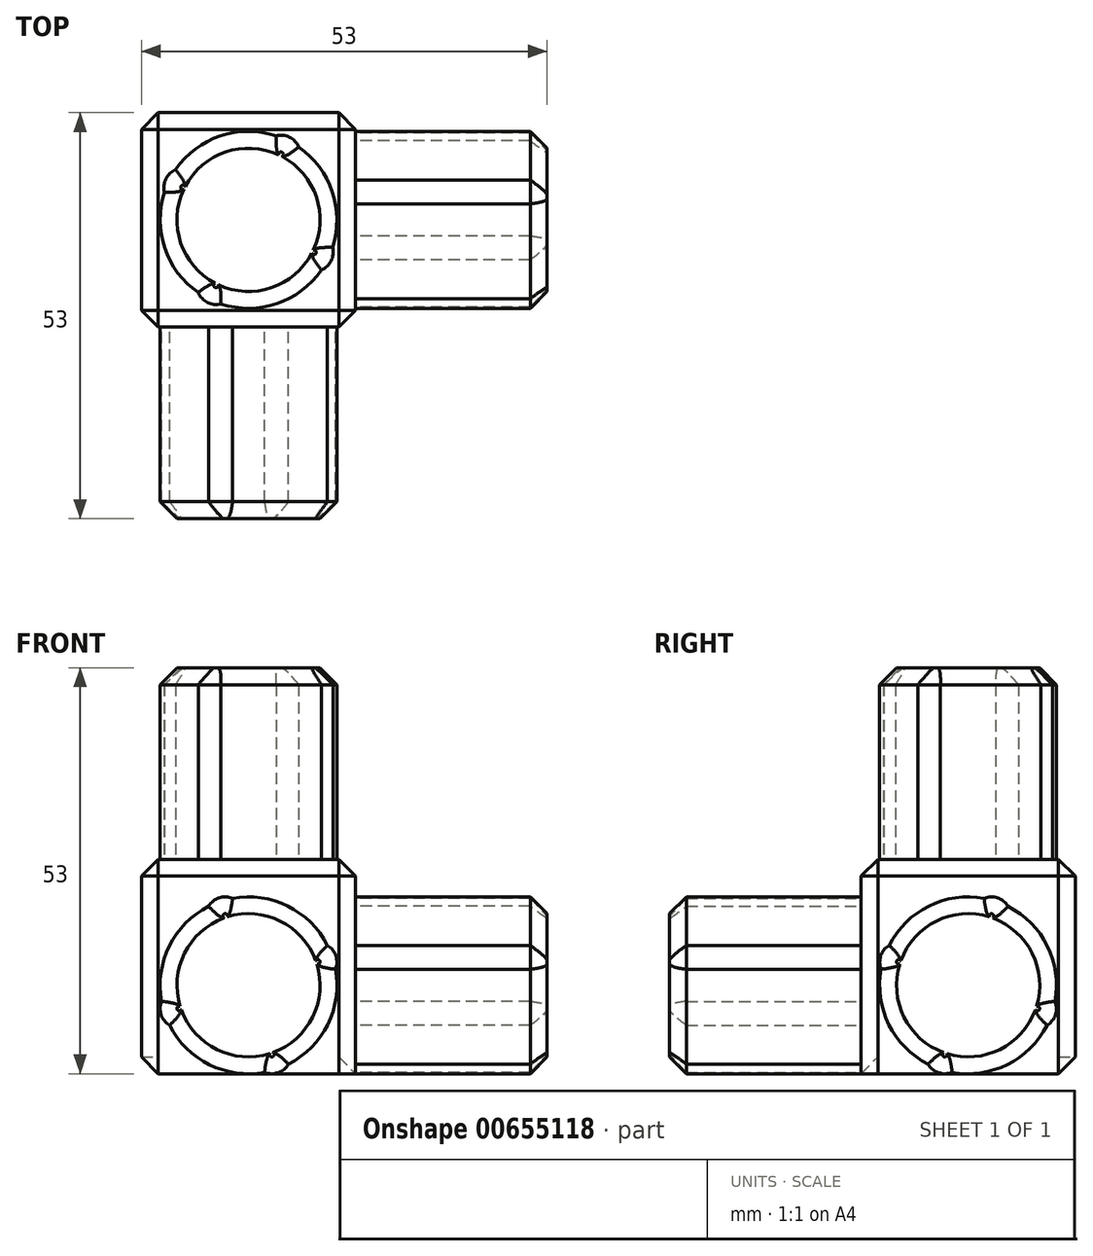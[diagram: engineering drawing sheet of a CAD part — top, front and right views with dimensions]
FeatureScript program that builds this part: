
annotation { "Feature Type Name" : "Feature", "Feature Type Description" : "" }
export const myFeature = defineFeature(function(context is Context, id is Id, definition is map)
    precondition{}
    {
        {
            var Q0;
            Q0=qCreatedBy(makeId("Front.planeOp"),FACE);
            var sketch = newSketch(context, id + "F0", { "sketchPlane" : qUnion([Q0])});
            skLineSegment(sketch, "E0.bottom", {"start": v(-14, 0) * mm, "end": v(14, 0) * mm});
            skLineSegment(sketch, "E0.top", {"start": v(-14, 28) * mm, "end": v(14, 28) * mm});
            skLineSegment(sketch, "E0.left", {"start": v(-14, 0) * mm, "end": v(-14, 28) * mm});
            skLineSegment(sketch, "E0.right", {"start": v(14, 0) * mm, "end": v(14, 28) * mm});
            skSolve(sketch);
        }
        {
            var Q0;
            Q0 = qSketchRegion(id + "F0", true);
            extrude(context, id + "F1", {"entities" : qUnion([Q0]), "depth" : 28 * mm, "offsetDistance" : 25 * mm, "symmetric" : true});
        }
        {
            var Q0;
            Q0=makeQuery(id+"F1.opExtrude","CAP_FACE",FACE,{"disambiguationData":[OSD([sQuery(id+"F0.wireOp",EDGE,"E0.bottom"),sQuery(id+"F0.wireOp",EDGE,"E0.top"),sQuery(id+"F0.wireOp",EDGE,"E0.left"),sQuery(id+"F0.wireOp",EDGE,"E0.right")])],"isStart":false});
            var sketch = newSketch(context, id + "F2", { "sketchPlane" : qUnion([Q0])});
            skArc(sketch, "E1", {"start": v(-10.3, 6.34) * mm, "mid": v(-5.13, 1.2) * mm, "end": v(2.1, 0.2) * mm});
            skArc(sketch, "E2", {"start": v(-11.36, 9.46) * mm, "mid": v(-11.42, 7.7) * mm, "end": v(-10.3, 6.34) * mm});
            skArc(sketch, "E3.1.0", {"start": v(2.1, 0.2) * mm, "mid": v(3.85, 0.13) * mm, "end": v(5.2, 1.24) * mm});
            skArc(sketch, "E3.2.0", {"start": v(11.36, 13.64) * mm, "mid": v(11.42, 15.4) * mm, "end": v(10.3, 16.76) * mm});
            skArc(sketch, "E4.1.3.0", {"start": v(-2.1, 22.9) * mm, "mid": v(-3.85, 22.97) * mm, "end": v(-5.2, 21.86) * mm});
            skArc(sketch, "E5.trimOffspring", {"start": v(-5.2, 21.86) * mm, "mid": v(-10.35, 16.68) * mm, "end": v(-11.36, 9.46) * mm});
            skArc(sketch, "E6.trimOffspring", {"start": v(10.3, 16.76) * mm, "mid": v(5.13, 21.9) * mm, "end": v(-2.1, 22.9) * mm});
            skArc(sketch, "E7.trimOffspring", {"start": v(5.2, 1.24) * mm, "mid": v(10.35, 6.42) * mm, "end": v(11.36, 13.64) * mm});
            skSolve(sketch);
        }
        {
            var Q0;
            Q0=makeQuery(id+"F2.imprint","IMPRINT",FACE,{"disambiguationData":[TD([[makeQuery(id+"F2.imprint","IMPRINT",EDGE,{"derivedFrom":sQuery(id+"F2.wireOp",EDGE,"E1")}),1.0]])]});
            extrude(context, id + "F3", {"entities" : qUnion([Q0]), "operationType" : NewBodyOperationType.ADD, "depth" : 25 * mm, "offsetDistance" : 25 * mm});
        }
        {
            var Q0;
            Q0=makeQuery(id+"F1.opExtrude","SWEPT_FACE",FACE,{"disambiguationData":[OSD([sQuery(id+"F0.wireOp",EDGE,"E0.right")])]});
            var sketch = newSketch(context, id + "F4", { "sketchPlane" : qUnion([Q0])});
            skArc(sketch, "E8", {"start": v(-11.36, 13.64) * mm, "mid": v(-10.35, 6.42) * mm, "end": v(-5.2, 1.24) * mm});
            skArc(sketch, "E9", {"start": v(-10.3, 16.76) * mm, "mid": v(-11.42, 15.4) * mm, "end": v(-11.36, 13.64) * mm});
            skArc(sketch, "E10.1.0", {"start": v(-5.2, 1.24) * mm, "mid": v(-3.85, 0.13) * mm, "end": v(-2.1, 0.2) * mm});
            skArc(sketch, "E10.2.0", {"start": v(10.3, 6.34) * mm, "mid": v(11.42, 7.7) * mm, "end": v(11.36, 9.46) * mm});
            skArc(sketch, "E10.3.0", {"start": v(5.2, 21.86) * mm, "mid": v(3.85, 22.97) * mm, "end": v(2.1, 22.9) * mm});
            skArc(sketch, "E11.trimOffspring", {"start": v(2.1, 22.9) * mm, "mid": v(-5.13, 21.9) * mm, "end": v(-10.3, 16.76) * mm});
            skArc(sketch, "E12.trimOffspring", {"start": v(11.36, 9.46) * mm, "mid": v(10.35, 16.68) * mm, "end": v(5.2, 21.86) * mm});
            skArc(sketch, "E13.trimOffspring", {"start": v(-2.1, 0.2) * mm, "mid": v(5.13, 1.2) * mm, "end": v(10.3, 6.34) * mm});
            skSolve(sketch);
        }
        {
            var Q0;
            Q0 = qSketchRegion(id + "F4", true);
            extrude(context, id + "F5", {"entities" : qUnion([Q0]), "operationType" : NewBodyOperationType.ADD, "depth" : 25 * mm, "offsetDistance" : 25 * mm});
        }
        {
            var Q0;
            Q0=makeQuery(id+"F1.opExtrude","SWEPT_FACE",FACE,{"disambiguationData":[OSD([sQuery(id+"F0.wireOp",EDGE,"E0.top")])]});
            var sketch = newSketch(context, id + "F6", { "sketchPlane" : qUnion([Q0])});
            skArc(sketch, "E14", {"start": v(-10.97, 3.6) * mm, "mid": v(-10.95, -3.69) * mm, "end": v(-6.55, -9.51) * mm});
            skArc(sketch, "E15", {"start": v(-9.51, 6.55) * mm, "mid": v(-10.8, 5.35) * mm, "end": v(-10.97, 3.6) * mm});
            skArc(sketch, "E16.1.0", {"start": v(-6.55, -9.51) * mm, "mid": v(-5.35, -10.8) * mm, "end": v(-3.6, -10.97) * mm});
            skArc(sketch, "E16.2.0", {"start": v(9.51, -6.55) * mm, "mid": v(10.8, -5.35) * mm, "end": v(10.97, -3.6) * mm});
            skArc(sketch, "E16.3.0", {"start": v(6.55, 9.51) * mm, "mid": v(5.35, 10.8) * mm, "end": v(3.6, 10.97) * mm});
            skArc(sketch, "E17.trimOffspring", {"start": v(-3.6, -10.97) * mm, "mid": v(3.69, -10.95) * mm, "end": v(9.51, -6.55) * mm});
            skArc(sketch, "E18.trimOffspring", {"start": v(10.97, -3.6) * mm, "mid": v(10.95, 3.69) * mm, "end": v(6.55, 9.51) * mm});
            skArc(sketch, "E19.trimOffspring", {"start": v(3.6, 10.97) * mm, "mid": v(-3.69, 10.95) * mm, "end": v(-9.51, 6.55) * mm});
            skSolve(sketch);
        }
        {
            var Q0;
            Q0=makeQuery(id+"F6.imprint","IMPRINT",FACE,{"disambiguationData":[TD([[makeQuery(id+"F6.imprint","IMPRINT",EDGE,{"derivedFrom":sQuery(id+"F6.wireOp",EDGE,"E14")}),1.0]])]});
            extrude(context, id + "F7", {"entities" : qUnion([Q0]), "operationType" : NewBodyOperationType.ADD, "depth" : 25 * mm, "offsetDistance" : 25 * mm});
        }
        {
            var Q0;
            Q0=makeQuery(id+"F5.opExtrude","CAP_EDGE",EDGE,{"disambiguationData":[OSD([sQuery(id+"F4.wireOp",EDGE,"E8")])],"isStart":false});
            var Q1;
            Q1=makeQuery(id+"F3.opExtrude","CAP_EDGE",EDGE,{"disambiguationData":[OSD([sQuery(id+"F2.wireOp",EDGE,"E1")])],"isStart":false});
            var Q2;
            Q2=makeQuery(id+"F7.opExtrude","CAP_EDGE",EDGE,{"disambiguationData":[OSD([sQuery(id+"F6.wireOp",EDGE,"E14")])],"isStart":false});
            var Q3;
            Q3=makeQuery(id+"F1.opExtrude","SWEPT_FACE",FACE,{"disambiguationData":[OSD([sQuery(id+"F0.wireOp",EDGE,"E0.left")])]});
            var Q4;
            Q4=makeQuery(id+"F1.opExtrude","CAP_FACE",FACE,{"disambiguationData":[OSD([sQuery(id+"F0.wireOp",EDGE,"E0.bottom"),sQuery(id+"F0.wireOp",EDGE,"E0.top"),sQuery(id+"F0.wireOp",EDGE,"E0.left"),sQuery(id+"F0.wireOp",EDGE,"E0.right")])],"isStart":true});
            var Q5;
            Q5=makeQuery(id+"F1.opExtrude","SWEPT_EDGE",EDGE,{"disambiguationData":[OSD([sQuery(id+"F0.wireOp",EDGE,"E0.top"),sQuery(id+"F0.wireOp",EDGE,"E0.right")])]});
            var Q6;
            Q6=makeQuery(id+"F1.opExtrude","CAP_EDGE",EDGE,{"disambiguationData":[OSD([sQuery(id+"F0.wireOp",EDGE,"E0.top")])],"isStart":false});
            var Q7;
            Q7=makeQuery(id+"F1.opExtrude","CAP_EDGE",EDGE,{"disambiguationData":[OSD([sQuery(id+"F0.wireOp",EDGE,"E0.right")])],"isStart":false});
            var Q8;
            Q8=makeQuery(id+"F3.opExtrude","CAP_EDGE",EDGE,{"disambiguationData":[OSD([sQuery(id+"F2.wireOp",EDGE,"E5.trimOffspring")])],"isStart":false});
            var Q9;
            Q9=makeQuery(id+"F3.opExtrude","CAP_EDGE",EDGE,{"disambiguationData":[OSD([sQuery(id+"F2.wireOp",EDGE,"E2")])],"isStart":false});
            var Q10;
            Q10=makeQuery(id+"F3.opExtrude","CAP_FACE",FACE,{"disambiguationData":[OSD([sQuery(id+"F2.wireOp",EDGE,"E1"),sQuery(id+"F2.wireOp",EDGE,"E2"),sQuery(id+"F2.wireOp",EDGE,"E3.1.0"),sQuery(id+"F2.wireOp",EDGE,"E3.2.0"),sQuery(id+"F2.wireOp",EDGE,"E4.1.3.0"),sQuery(id+"F2.wireOp",EDGE,"E5.trimOffspring"),sQuery(id+"F2.wireOp",EDGE,"E6.trimOffspring"),sQuery(id+"F2.wireOp",EDGE,"E7.trimOffspring")])],"isStart":false});
            var Q11;
            Q11=makeQuery(id+"F5.opExtrude","CAP_FACE",FACE,{"disambiguationData":[OSD([sQuery(id+"F4.wireOp",EDGE,"E8"),sQuery(id+"F4.wireOp",EDGE,"E9"),sQuery(id+"F4.wireOp",EDGE,"E10.1.0"),sQuery(id+"F4.wireOp",EDGE,"E10.2.0"),sQuery(id+"F4.wireOp",EDGE,"E10.3.0"),sQuery(id+"F4.wireOp",EDGE,"E11.trimOffspring"),sQuery(id+"F4.wireOp",EDGE,"E12.trimOffspring"),sQuery(id+"F4.wireOp",EDGE,"E13.trimOffspring")])],"isStart":false});
            var Q12;
            Q12=makeQuery(id+"F7.opExtrude","CAP_FACE",FACE,{"disambiguationData":[OSD([sQuery(id+"F6.wireOp",EDGE,"E14"),sQuery(id+"F6.wireOp",EDGE,"E15"),sQuery(id+"F6.wireOp",EDGE,"E16.1.0"),sQuery(id+"F6.wireOp",EDGE,"E16.2.0"),sQuery(id+"F6.wireOp",EDGE,"E16.3.0"),sQuery(id+"F6.wireOp",EDGE,"E17.trimOffspring"),sQuery(id+"F6.wireOp",EDGE,"E18.trimOffspring"),sQuery(id+"F6.wireOp",EDGE,"E19.trimOffspring")])],"isStart":false});
            chamfer(context, id + "F8", {"entities" : qUnion([Q0, Q1, Q2, Q3, Q4, Q5, Q6, Q7, Q8, Q9, Q10, Q11, Q12]), "width" : 2.2 * mm, "tangentPropagation" : true});
        }
    });
